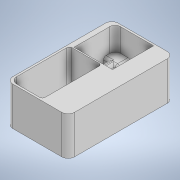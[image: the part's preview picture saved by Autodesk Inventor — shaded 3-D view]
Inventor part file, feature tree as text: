
AUTODESK INVENTOR PART (.ipt)
format: ipt  version: 2022 (Build 260153000, 153)  size: 220,672 bytes
history: native  units: mm
features: extrude x5, sketch x5, fillet x1
ambient origin geometry x8: Origin, YZ Plane, XZ Plane, XY Plane, X Axis, Y Axis, Z Axis, Center Point
bodies: Solid1 (feature_tree)
feature tree (11):
  extrude  "Extrusion1"  Depth=82.0mm
  extrude  "Extrusion4"  Depth=24.0mm
  extrude  "Extrusion6"  Depth=30.0mm TaperAngle=0.0deg
  extrude  "Extrusion7"  Depth=1.5mm
  extrude  "Extrusion8"  Depth=2.0mm
  fillet  "Fillet1"  Radius=25.0mm
  sketch  "Sketch1"  dims[d0=48.0mm d1=82.0mm]
  sketch  "Sketch5"  dims[d2=41.0mm d3=24.0mm]
  sketch  "Sketch7"  dims[d5=5.0mm d6=30.0mm d7=0.0mm]
  sketch  "Sketch8"  dims[d39=1.5mm d40=1.5mm]
  sketch  "Sketch9"  dims[d41=5.0mm d42=2.0mm d43=25.0mm d44=46.0mm d45=28.5mm d46=0.0mm d53=30.0mm d54=32.0mm d55=1.0mm d56=4.0mm d57=1.5mm d58=4.0mm d59=18.0mm d60=0.0mm d62=6.0mm d63=12.0mm d64=12.0mm d65=3.0mm d66=4.5mm d67=11.0mm d68=23.0mm d69=4.0mm d70=11.0mm d71=22.0mm d72=11.0mm d73=7.5mm d74=8.0mm d75=0.0mm d76=0.0mm d77=0.0mm d78=2.0mm]
